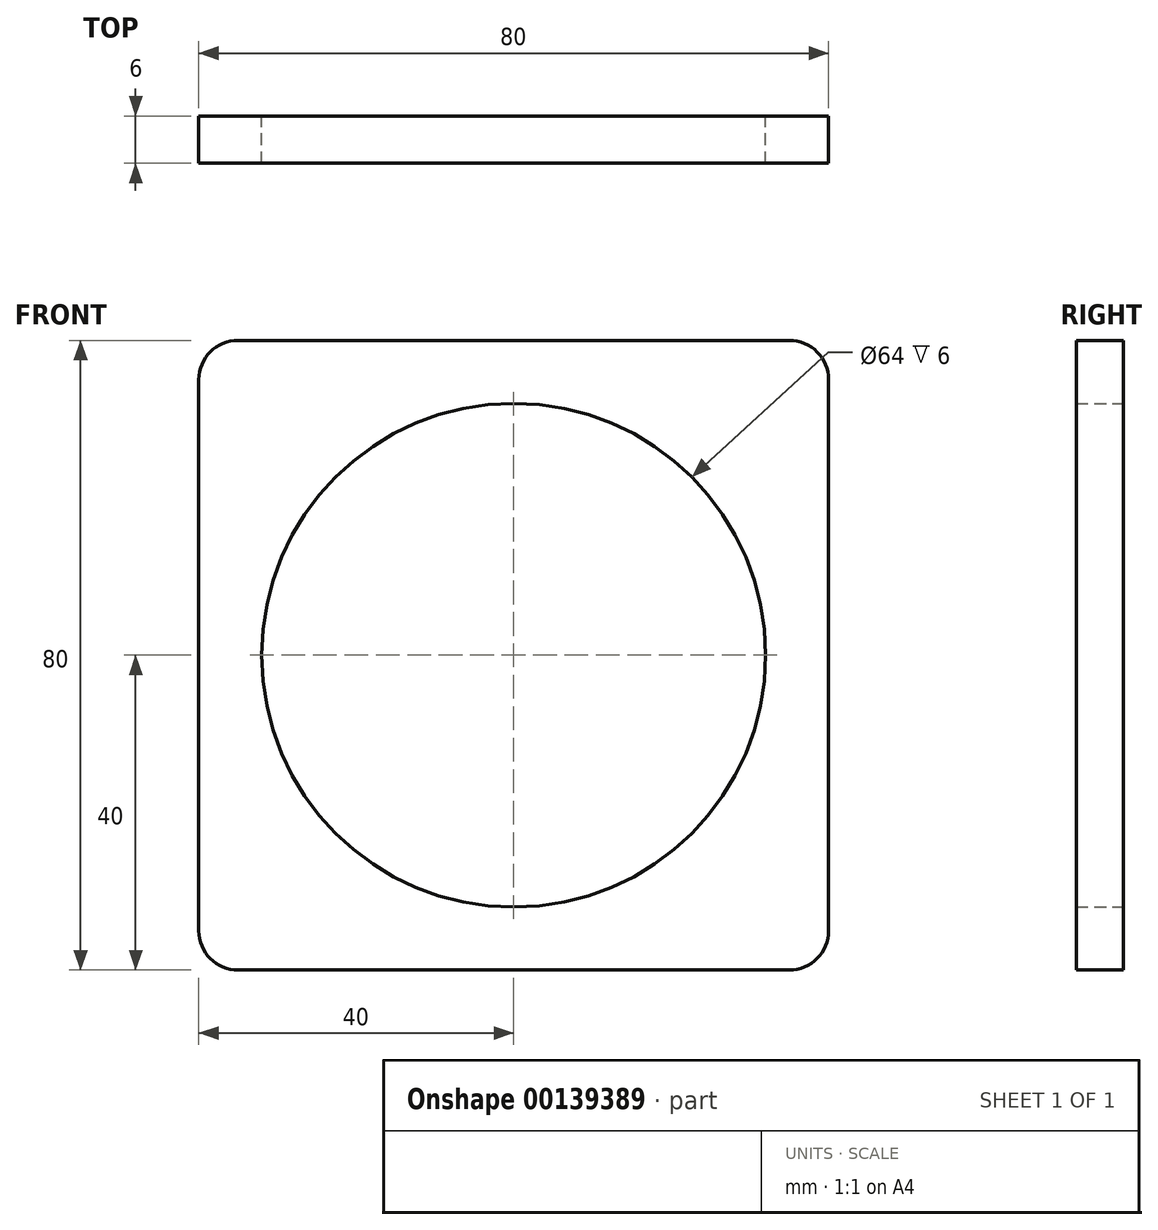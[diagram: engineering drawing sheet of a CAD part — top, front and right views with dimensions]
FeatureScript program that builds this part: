
annotation { "Feature Type Name" : "Feature", "Feature Type Description" : "" }
export const myFeature = defineFeature(function(context is Context, id is Id, definition is map)
    precondition{}
    {
        {
            var Q0;
            Q0=qCreatedBy(makeId("Front.planeOp"),FACE);
            var sketch = newSketch(context, id + "F0", { "sketchPlane" : qUnion([Q0])});
            skLineSegment(sketch, "E0.bottom", {"start": v(-5, 0) * mm, "end": v(-75, 0) * mm});
            skLineSegment(sketch, "E0.top", {"start": v(-5, 80) * mm, "end": v(-75, 80) * mm});
            skLineSegment(sketch, "E0.left", {"start": v(0, 5) * mm, "end": v(0, 75) * mm});
            skLineSegment(sketch, "E0.right", {"start": v(-80, 5) * mm, "end": v(-80, 75) * mm});
            skPoint(sketch, "E1.visualSharp", {"position": v(-80, 80) * mm});
            skArc(sketch, "E1.filletArc", {"start": v(-75, 80) * mm, "mid": v(-78.54, 78.54) * mm, "end": v(-80, 75) * mm});
            skPoint(sketch, "E2.visualSharp", {"position": v(0, 80) * mm});
            skArc(sketch, "E2.filletArc", {"start": v(0, 75) * mm, "mid": v(-1.46, 78.54) * mm, "end": v(-5, 80) * mm});
            skPoint(sketch, "E3.visualSharp", {"position": v(-80, 0) * mm});
            skArc(sketch, "E3.filletArc", {"start": v(-80, 5) * mm, "mid": v(-78.54, 1.46) * mm, "end": v(-75, 0) * mm});
            skPoint(sketch, "E4.visualSharp", {"position": v(0, 0) * mm});
            skArc(sketch, "E4.filletArc", {"start": v(-5, 0) * mm, "mid": v(-1.46, 1.46) * mm, "end": v(0, 5) * mm});
            skPoint(sketch, "E5.visualSharp", {"position": v(-65, 5) * mm});
            skCircle(sketch, "E6", {"center": v(-40, 40) * mm, "radius": 32 * mm});
            skSolve(sketch);
        }
        {
            var Q0;
            Q0=makeQuery(id+"F0.imprint","IMPRINT",FACE,{"disambiguationData":[TD([[makeQuery(id+"F0.imprint","IMPRINT",EDGE,{"derivedFrom":sQuery(id+"F0.wireOp",EDGE,"E0.bottom")}),-1.0]])]});
            extrude(context, id + "F1", {"entities" : qUnion([Q0]), "depth" : 6 * mm});
        }
    });
